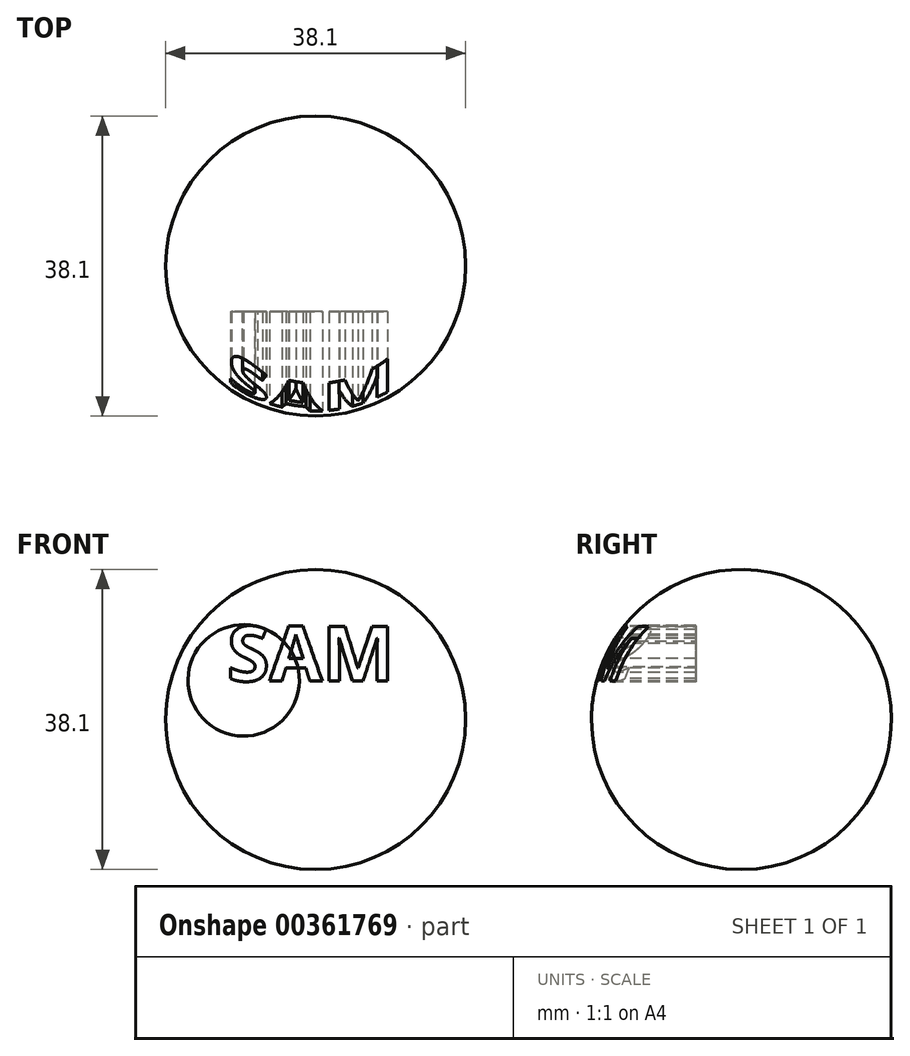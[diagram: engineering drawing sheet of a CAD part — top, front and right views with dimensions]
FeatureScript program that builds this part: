
annotation { "Feature Type Name" : "Feature", "Feature Type Description" : "" }
export const myFeature = defineFeature(function(context is Context, id is Id, definition is map)
    precondition{}
    {
        {
            var Q0;
            Q0=qCreatedBy(makeId("Top.planeOp"),FACE);
            var sketch = newSketch(context, id + "F0", { "sketchPlane" : qUnion([Q0])});
            skLineSegment(sketch, "E0", {"start": v(-29.78, 12.12) * mm, "end": v(-29.78, -25.98) * mm});
            skLineSegment(sketch, "E1", {"start": v(-29.78, -25.98) * mm, "end": v(8.32, -25.98) * mm});
            skLineSegment(sketch, "E2", {"start": v(8.32, -25.98) * mm, "end": v(8.32, 12.12) * mm});
            skLineSegment(sketch, "E3", {"start": v(-29.78, 12.12) * mm, "end": v(8.32, 12.12) * mm});
            skSolve(sketch);
        }
        {
            var Q0;
            Q0=makeQuery(id+"F0.imprint","IMPRINT",FACE,{"disambiguationData":[TD([[makeQuery(id+"F0.imprint","IMPRINT",EDGE,{"derivedFrom":sQuery(id+"F0.wireOp",EDGE,"E0")}),1.0]])]});
            extrude(context, id + "F1", {"entities" : qUnion([Q0]), "depth" : 38.1 * mm});
        }
        {
            var Q0;
            Q0=makeQuery(id+"F1.opExtrude","CAP_FACE",FACE,{"disambiguationData":[OSD([sQuery(id+"F0.wireOp",EDGE,"E0"),sQuery(id+"F0.wireOp",EDGE,"E1"),sQuery(id+"F0.wireOp",EDGE,"E2"),sQuery(id+"F0.wireOp",EDGE,"E3")])],"isStart":false});
            var Q1;
            Q1=makeQuery(id+"F1.opExtrude","SWEPT_FACE",FACE,{"disambiguationData":[OSD([sQuery(id+"F0.wireOp",EDGE,"E3")])]});
            var Q2;
            Q2=makeQuery(id+"F1.opExtrude","SWEPT_FACE",FACE,{"disambiguationData":[OSD([sQuery(id+"F0.wireOp",EDGE,"E2")])]});
            var Q3;
            Q3=makeQuery(id+"F1.opExtrude","CAP_FACE",FACE,{"disambiguationData":[OSD([sQuery(id+"F0.wireOp",EDGE,"E0"),sQuery(id+"F0.wireOp",EDGE,"E1"),sQuery(id+"F0.wireOp",EDGE,"E2"),sQuery(id+"F0.wireOp",EDGE,"E3")])],"isStart":true});
            var Q4;
            Q4=makeQuery(id+"F1.opExtrude","SWEPT_FACE",FACE,{"disambiguationData":[OSD([sQuery(id+"F0.wireOp",EDGE,"E0")])]});
            fillet(context, id + "F2", {"entities" : qUnion([Q0, Q1, Q2, Q3, Q4]), "radius" : 19.05 * mm, "tangentPropagation" : true, "allowEdgeOverflow" : false});
        }
        {
            var Q0;
            Q0=qCreatedBy(makeId("Front.planeOp"),FACE);
            cPlane(context, id + "F3", {"entities" : qUnion([Q0]), "cplaneType" : CPlaneType.OFFSET, "offset" : 25.4 * mm, "width" : 152.4 * mm, "height" : 152.4 * mm});
        }
        {
            var Q0;
            Q0=qCreatedBy(id+"F3.planeOp",FACE);
            var sketch = newSketch(context, id + "F4", { "sketchPlane" : qUnion([Q0])});
            skText(sketch, "E4", { "text": "SAM", "fontName": "OpenSans-Bold.ttf"});
            const initialGuessF4  = {"E4": [-0.02195, 0.02393, 1, 0, 0.00701]};
            skSetInitialGuess(sketch, initialGuessF4);
            skSolve(sketch);
        }
        {
            var Q0;
            Q0=makeQuery(id+"F4.imprint","IMPRINT",FACE,{"disambiguationData":[TD([[makeQuery(id+"F4.imprint","IMPRINT",EDGE,{"derivedFrom":sQuery(id+"F4.wireOp",EDGE,"cc7d2541-04ae-4529-a4a9-c8720d162468.sketch_text.stroke-0")}),-1.0]])]});
            var Q1;
            Q1=makeQuery(id+"F4.imprint","IMPRINT",FACE,{"disambiguationData":[TD([[makeQuery(id+"F4.imprint","IMPRINT",EDGE,{"derivedFrom":sQuery(id+"F4.wireOp",EDGE,"cc7d2541-04ae-4529-a4a9-c8720d162468.sketch_text.stroke-53")}),-1.0]])]});
            var Q2;
            Q2=makeQuery(id+"F4.imprint","IMPRINT",FACE,{"disambiguationData":[TD([[makeQuery(id+"F4.imprint","IMPRINT",EDGE,{"derivedFrom":sQuery(id+"F4.wireOp",EDGE,"cc7d2541-04ae-4529-a4a9-c8720d162468.sketch_text.stroke-81")}),-1.0]])]});
            var Q3;
            Q3=makeQuery(id+"F4.imprint","IMPRINT",FACE,{"disambiguationData":[TD([[makeQuery(id+"F4.imprint","IMPRINT",EDGE,{"derivedFrom":sQuery(id+"F4.wireOp",EDGE,"cc7d2541-04ae-4529-a4a9-c8720d162468.sketch_text.stroke-118")}),-1.0]])]});
            var Q4;
            Q4=makeQuery(id+"F4.imprint","IMPRINT",FACE,{"disambiguationData":[TD([[makeQuery(id+"F4.imprint","IMPRINT",EDGE,{"derivedFrom":sQuery(id+"F4.wireOp",EDGE,"cc7d2541-04ae-4529-a4a9-c8720d162468.sketch_text.stroke-28")}),-1.0]])]});
            var Q5;
            Q5=makeQuery(id+"F4.imprint","IMPRINT",FACE,{"disambiguationData":[TD([[makeQuery(id+"F4.imprint","IMPRINT",EDGE,{"derivedFrom":sQuery(id+"F4.wireOp",EDGE,"cc7d2541-04ae-4529-a4a9-c8720d162468.sketch_text.stroke-98")}),-1.0]])]});
            var Q6;
            Q6 = qSketchRegion(id + "F4", true);
            var Q7;
            Q7=makeQuery(id+"F4.imprint","IMPRINT",FACE,{"disambiguationData":[TD([[makeQuery(id+"F4.imprint","IMPRINT",EDGE,{"derivedFrom":sQuery(id+"F4.wireOp",EDGE,"cc7d2541-04ae-4529-a4a9-c8720d162468.sketch_text.stroke-46")}),1.0]])]});
            extrude(context, id + "F5", {"entities" : qUnion([Q0, Q1, Q2, Q3, Q4, Q5, Q6, Q7]), "operationType" : NewBodyOperationType.REMOVE, "oppositeDirection" : true, "depth" : 12.7 * mm});
        }
    });
